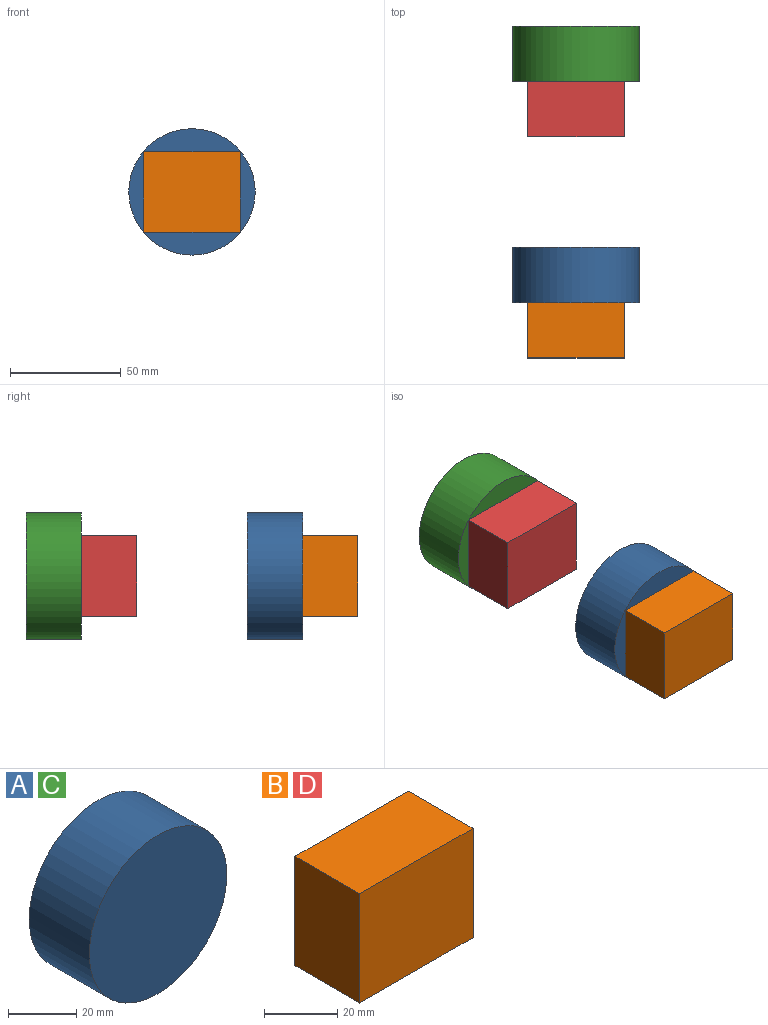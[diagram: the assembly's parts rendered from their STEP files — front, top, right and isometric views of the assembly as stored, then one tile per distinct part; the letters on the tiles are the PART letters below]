
ASSEMBLY  parts=4 mates=1
PART A: 3 faces, bbox 57.1x25x57.1 mm
  f0: cylinder r=28.56mm len=57.12mm, axis (0,1,0), area 4485.9mm2, adj f1,f2
  f1: plane 57.12x57.12mm, normal (0,-1,0), area 2562.2mm2, adj f0
  f2: plane 57.12x57.12mm, normal (0,1,0), area 2562.2mm2, adj f0
PART B: 6 faces, bbox 43.7x25x36.5 mm
  f0: plane 43.7x25mm, normal (0,0,1), area 1092.6mm2, adj f1,f3,f4,f5
  f1: plane 36.49x25mm, normal (-1,0,0), area 912.3mm2, adj f0,f2,f4,f5
  f2: plane 43.7x25mm, normal (0,0,-1), area 1092.6mm2, adj f1,f3,f4,f5
  f3: plane 36.49x25mm, normal (1,0,0), area 912.3mm2, adj f0,f2,f4,f5
  f4: plane 43.7x36.49mm, normal (0,-1,0), area 1594.8mm2, adj f0,f1,f2,f3
  f5: plane 43.7x36.49mm, normal (0,1,0), area 1594.8mm2, adj f0,f1,f2,f3
PART C: same geometry as A
PART D: same geometry as B
PLACE A at identity
PLACE B rot(axis=(1,0,0),180deg) t=(178.51,-50,26.18)mm
PLACE C t=(0,100,0)mm
PLACE D rot(axis=(1,0,0),180deg) t=(178.51,50,26.18)mm
MATE revolute B.f4 <-> A.f0  axis (0,1,0) through (75.81,-25,7.93)mm
